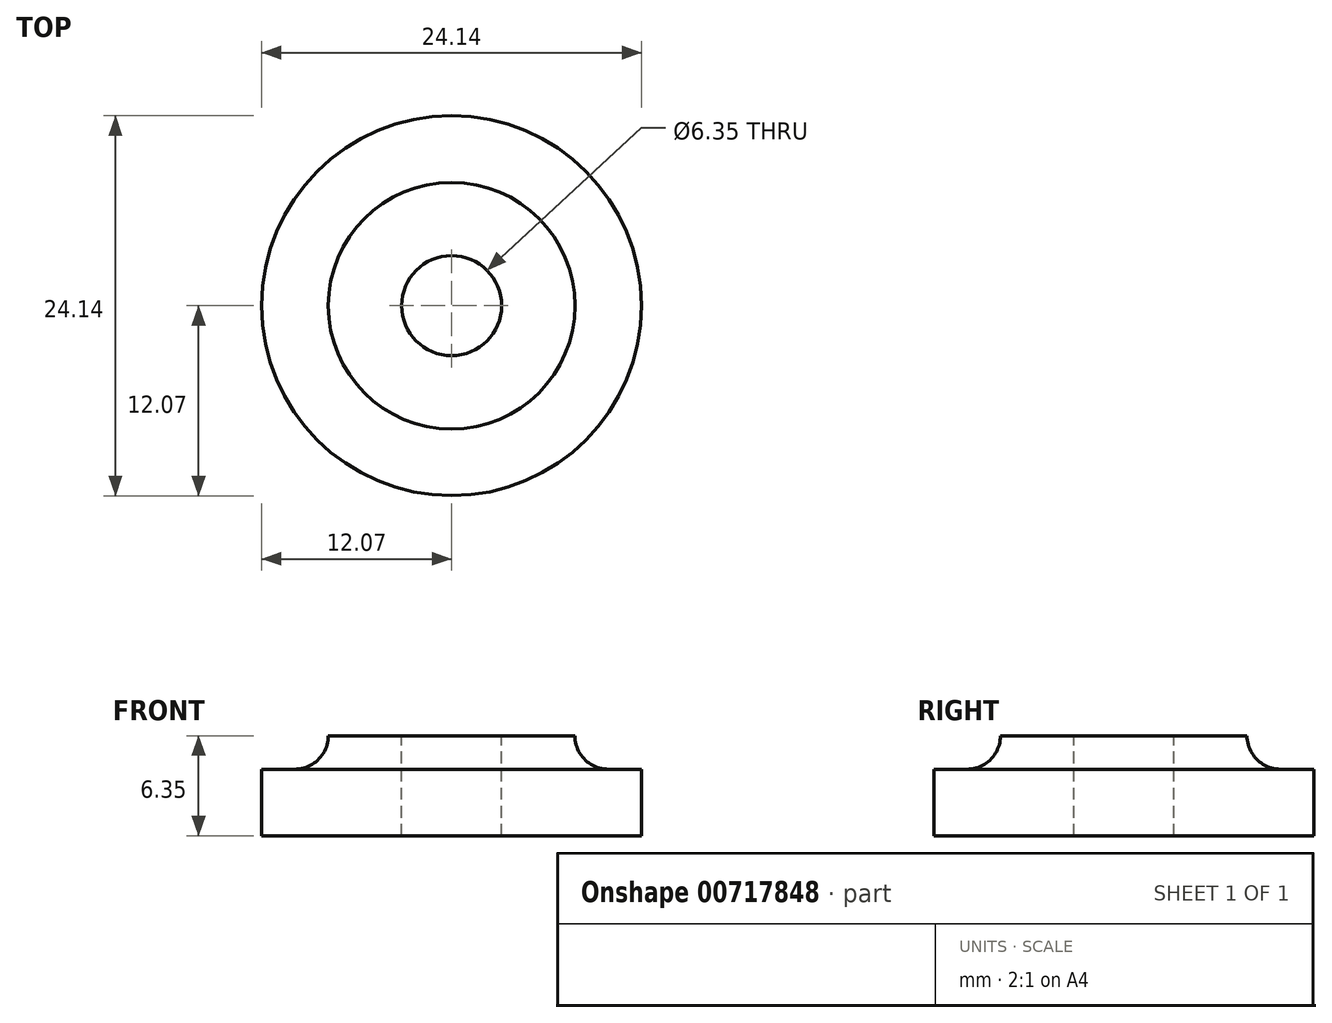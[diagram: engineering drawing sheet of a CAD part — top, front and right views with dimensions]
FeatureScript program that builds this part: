
annotation { "Feature Type Name" : "Feature", "Feature Type Description" : "" }
export const myFeature = defineFeature(function(context is Context, id is Id, definition is map)
    precondition{}
    {
        {
            var Q0;
            Q0=qCreatedBy(makeId("Top.planeOp"),FACE);
            var sketch = newSketch(context, id + "F0", { "sketchPlane" : qUnion([Q0])});
            skCircle(sketch, "E0", {"center": v(0, 0) * mm, "radius": 15.88 * mm});
            skSolve(sketch);
        }
        {
            var Q0;
            Q0 = qSketchRegion(id + "F0", true);
            extrude(context, id + "F1", {"entities" : qUnion([Q0]), "depth" : 12.7 * mm, "offsetDistance" : 25.4 * mm});
        }
        {
            var Q0;
            Q0=qCreatedBy(makeId("Right.planeOp"),FACE);
            var sketch = newSketch(context, id + "F2", { "sketchPlane" : qUnion([Q0])});
            skLineSegment(sketch, "E1", {"start": v(0, 0) * mm, "end": v(-12.07, 0) * mm});
            skLineSegment(sketch, "E2", {"start": v(-12.07, 4.23) * mm, "end": v(-12.07, 8.47) * mm});
            skLineSegment(sketch, "E3", {"start": v(-12.07, 12.7) * mm, "end": v(-13.76, 12.7) * mm});
            skArc(sketch, "E4", {"start": v(-9.95, 4.23) * mm, "mid": v(-7.83, 6.35) * mm, "end": v(-9.95, 8.47) * mm});
            skLineSegment(sketch, "E5", {"start": v(-9.95, 8.47) * mm, "end": v(-12.06, 8.47) * mm});
            skLineSegment(sketch, "E6", {"start": v(-9.95, 4.23) * mm, "end": v(-12.07, 4.23) * mm});
            skPoint(sketch, "E7.orphan", {"position": v(-13.76, 0) * mm});
            skSolve(sketch);
        }
        {
            var Q0;
            Q0=qCreatedBy(makeId("Right.planeOp"),FACE);
            var sketch = newSketch(context, id + "F3", { "sketchPlane" : qUnion([Q0])});
            skLineSegment(sketch, "E8", {"start": v(0, 0) * mm, "end": v(0, 22.83) * mm});
            skSolve(sketch);
        }
        {
            var Q0;
            Q0 = qSketchRegion(id + "F2", true);
            var Q1;
            Q1=sQuery(id+"F3.wireOp",EDGE,"E8");
            revolve(context, id + "F4", {"operationType" : NewBodyOperationType.REMOVE, "surfaceOperationType" : NewSurfaceOperationType.NEW, "entities" : qUnion([Q0]), "axis" : qUnion([Q1]), "revolveType" : RevolveType.FULL, "oppositeDirection" : true});
        }
        {
            var Q0;
            Q0=makeQuery(id+"F1.opExtrude","CAP_FACE",FACE,{"disambiguationData":[OSD([sQuery(id+"F0.wireOp",EDGE,"E0")])],"isStart":false});
            var sketch = newSketch(context, id + "F5", { "sketchPlane" : qUnion([Q0])});
            skCircle(sketch, "E9", {"center": v(0, 0) * mm, "radius": 3.18 * mm});
            skSolve(sketch);
        }
        {
            var Q0;
            Q0 = qSketchRegion(id + "F5", true);
            extrude(context, id + "F6", {"entities" : qUnion([Q0]), "operationType" : NewBodyOperationType.REMOVE, "endBound" : BoundingType.THROUGH_ALL, "oppositeDirection" : true, "depth" : 25.4 * mm, "offsetDistance" : 25.4 * mm});
        }
        {
            var Q0;
            Q0=makeQuery(id+"F1.opExtrude","CAP_FACE",FACE,{"disambiguationData":[OSD([sQuery(id+"F0.wireOp",EDGE,"E0")])],"isStart":false});
            var sketch = newSketch(context, id + "F7", { "sketchPlane" : qUnion([Q0])});
            skCircle(sketch, "E10", {"center": v(0, 0) * mm, "radius": 12.06 * mm});
            skCircle(sketch, "E11", {"center": v(0, 0) * mm, "radius": 20.02 * mm});
            skSolve(sketch);
        }
        {
            var Q0;
            Q0 = qSketchRegion(id + "F7", true);
            extrude(context, id + "F8", {"entities" : qUnion([Q0]), "operationType" : NewBodyOperationType.REMOVE, "endBound" : BoundingType.THROUGH_ALL, "oppositeDirection" : true, "depth" : 25.4 * mm, "offsetDistance" : 25.4 * mm});
        }
        {
            var Q0;
            Q0=qCreatedBy(makeId("Top.planeOp"),FACE);
            cPlane(context, id + "F9", {"entities" : qUnion([Q0]), "cplaneType" : CPlaneType.OFFSET, "offset" : 6.35 * mm, "width" : 152.4 * mm, "height" : 152.4 * mm});
        }
        {
            var Q0;
            Q0=makeQuery(id+"F1.opExtrude","CAP_FACE",FACE,{"disambiguationData":[OSD([sQuery(id+"F0.wireOp",EDGE,"E0")])],"isStart":false});
            var sketch = newSketch(context, id + "F10", { "sketchPlane" : qUnion([Q0])});
            skCircle(sketch, "E12", {"center": v(0, 0) * mm, "radius": 20.45 * mm});
            skCircle(sketch, "E13", {"center": v(0, 0) * mm, "radius": 1.77 * mm});
            skSolve(sketch);
        }
        {
            var Q0;
            Q0 = qSketchRegion(id + "F10", true);
            var Q1;
            Q1=qCreatedBy(id+"F9.planeOp",FACE);
            extrude(context, id + "F11", {"entities" : qUnion([Q0]), "operationType" : NewBodyOperationType.REMOVE, "endBound" : BoundingType.UP_TO_SURFACE, "oppositeDirection" : true, "depth" : 25.4 * mm, "endBoundEntityFace" : qUnion([Q1]), "offsetDistance" : 25.4 * mm});
        }
    });
